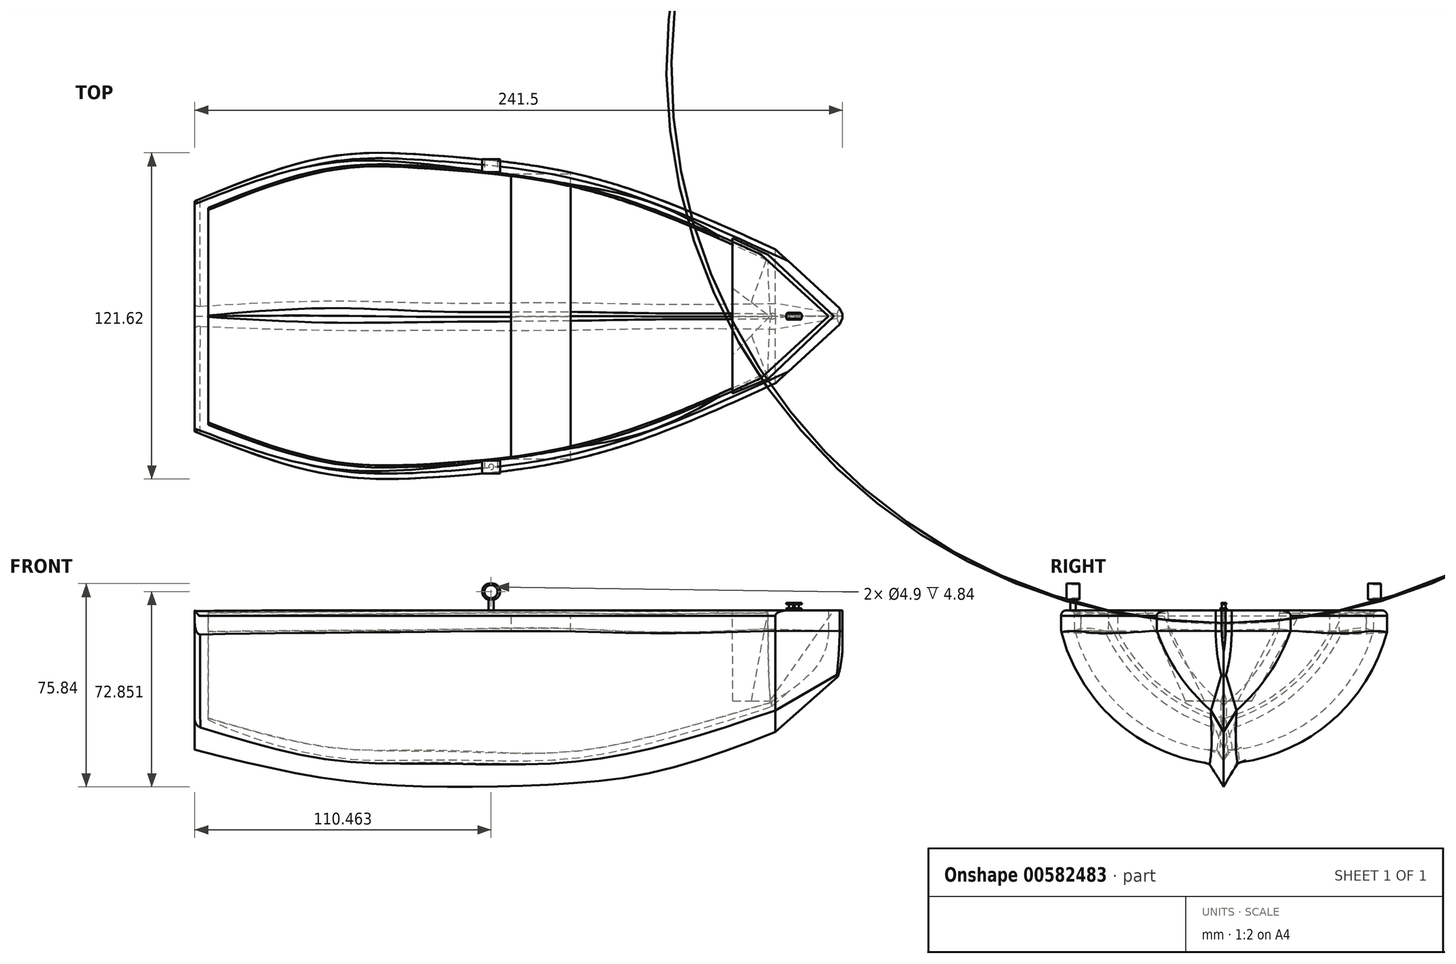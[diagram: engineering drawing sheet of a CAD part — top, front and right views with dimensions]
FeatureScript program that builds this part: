
annotation { "Feature Type Name" : "Feature", "Feature Type Description" : "" }
export const myFeature = defineFeature(function(context is Context, id is Id, definition is map)
    precondition{}
    {
        {
            var Q0;
            Q0=qCreatedBy(makeId("Right.planeOp"),FACE);
            var sketch = newSketch(context, id + "F0", { "sketchPlane" : qUnion([Q0])});
            skArc(sketch, "E0", {"start": v(-60, 57.64) * mm, "mid": v(-30.31, 51.1) * mm, "end": v(0, 48.9) * mm});
            skLineSegment(sketch, "E1", {"start": v(-59.87, 48.64) * mm, "end": v(-60, 57.64) * mm});
            skArc(sketch, "E2", {"start": v(-59.87, 48.64) * mm, "mid": v(-39.75, 16) * mm, "end": v(-5.17, -0.56) * mm});
            skArc(sketch, "E3.MirrorCS", {"start": v(60, 57.64) * mm, "mid": v(30.31, 51.1) * mm, "end": v(0, 48.9) * mm});
            skArc(sketch, "E4.MirrorCS", {"start": v(59.87, 48.64) * mm, "mid": v(39.55, 16.29) * mm, "end": v(4.98, 0) * mm});
            skLineSegment(sketch, "E5.MirrorCS", {"start": v(59.87, 48.64) * mm, "end": v(60, 57.64) * mm});
            skLineSegment(sketch, "E6", {"start": v(-5.17, -0.56) * mm, "end": v(0, -9.15) * mm});
            skLineSegment(sketch, "E7.MirrorCS", {"start": v(4.98, 0) * mm, "end": v(0, -9.15) * mm});
            skSolve(sketch);
        }
        {
            var Q0;
            {var subQ4=sQuery(id+"F0.wireOp",EDGE,"E1");Q0=makeQuery(id+"F0.imprint","IMPRINT",FACE,{"disambiguationData":[TD([[makeQuery(id+"F0.imprint","IMPRINT",EDGE,{"derivedFrom":subQ4}),-1.0]])]});}
            cPlane(context, id + "F1", {"entities" : qUnion([Q0]), "cplaneType" : CPlaneType.OFFSET, "offset" : 35 * mm, "oppositeDirection" : true, "width" : 150 * mm, "height" : 150 * mm});
        }
        {
            var Q0;
            Q0=qCreatedBy(id+"F1.planeOp",FACE);
            var sketch = newSketch(context, id + "F2", { "sketchPlane" : qUnion([Q0])});
            skArc(sketch, "E8", {"start": v(-59.74, 57.34) * mm, "mid": v(-30.06, 50.79) * mm, "end": v(0.26, 48.59) * mm});
            skLineSegment(sketch, "E9", {"start": v(-59.61, 48.34) * mm, "end": v(-59.74, 57.34) * mm});
            skArc(sketch, "E10", {"start": v(-59.61, 48.34) * mm, "mid": v(-39.35, 16.5) * mm, "end": v(-5.24, 0.36) * mm});
            skArc(sketch, "E11.MirrorCS", {"start": v(60.25, 57.34) * mm, "mid": v(30.57, 50.79) * mm, "end": v(0.26, 48.59) * mm});
            skArc(sketch, "E12.MirrorCS", {"start": v(60.13, 48.34) * mm, "mid": v(39.87, 16.5) * mm, "end": v(5.75, 0.36) * mm});
            skLineSegment(sketch, "E13.MirrorCS", {"start": v(60.13, 48.34) * mm, "end": v(60.25, 57.34) * mm});
            skLineSegment(sketch, "E14", {"start": v(-5.24, 0.36) * mm, "end": v(0, -6.9) * mm});
            skLineSegment(sketch, "E15.MirrorCS", {"start": v(5.75, 0.36) * mm, "end": v(5.75, 0.36) * mm});
            skLineSegment(sketch, "E16", {"start": v(5.75, 0.36) * mm, "end": v(0, -6.9) * mm});
            skSolve(sketch);
        }
        {
            var Q0;
            {var subQ4=sQuery(id+"F2.wireOp",EDGE,"E9");Q0=makeQuery(id+"F2.imprint","IMPRINT",FACE,{"disambiguationData":[TD([[makeQuery(id+"F2.imprint","IMPRINT",EDGE,{"derivedFrom":subQ4}),-1.0]])]});}
            cPlane(context, id + "F3", {"entities" : qUnion([Q0]), "cplaneType" : CPlaneType.OFFSET, "offset" : 55 * mm, "oppositeDirection" : true, "width" : 150 * mm, "height" : 150 * mm});
        }
        {
            var Q0;
            Q0=qCreatedBy(id+"F3.planeOp",FACE);
            var sketch = newSketch(context, id + "F4", { "sketchPlane" : qUnion([Q0])});
            skLineSegment(sketch, "E17", {"start": v(3.65, 13.62) * mm, "end": v(0, 4.64) * mm});
            skArc(sketch, "E18", {"start": v(-0.02, 51.89) * mm, "mid": v(21.6, 53.12) * mm, "end": v(42.98, 56.6) * mm});
            skArc(sketch, "E19.MirrorCS", {"start": v(0.02, 51.89) * mm, "mid": v(-21.6, 53.12) * mm, "end": v(-42.98, 56.6) * mm});
            skLineSegment(sketch, "E20.MirrorCS", {"start": v(-3.65, 13.62) * mm, "end": v(0, 4.64) * mm});
            skLineSegment(sketch, "E21", {"start": v(-42.98, 56.6) * mm, "end": v(-42.98, 47.6) * mm});
            skLineSegment(sketch, "E22", {"start": v(42.98, 56.6) * mm, "end": v(42.98, 47.6) * mm});
            skArc(sketch, "E23", {"start": v(3.65, 13.62) * mm, "mid": v(26.69, 26.7) * mm, "end": v(42.98, 47.6) * mm});
            skPoint(sketch, "E24.orphan", {"position": v(53.06, 38.96) * mm});
            skArc(sketch, "E25", {"start": v(-42.98, 47.6) * mm, "mid": v(-26.74, 26.64) * mm, "end": v(-3.65, 13.62) * mm});
            skPoint(sketch, "E26.orphan", {"position": v(-53.06, 38.96) * mm});
            skSolve(sketch);
        }
        {
            var Q0;
            Q0=qCreatedBy(makeId("Right.planeOp"),FACE);
            cPlane(context, id + "F5", {"entities" : qUnion([Q0]), "cplaneType" : CPlaneType.OFFSET, "offset" : 50 * mm, "width" : 150 * mm, "height" : 150 * mm});
        }
        {
            var Q0;
            Q0=qCreatedBy(id+"F5.planeOp",FACE);
            var sketch = newSketch(context, id + "F6", { "sketchPlane" : qUnion([Q0])});
            skArc(sketch, "E27", {"start": v(-53.66, 57.72) * mm, "mid": v(-27.06, 52.31) * mm, "end": v(0, 50.23) * mm});
            skLineSegment(sketch, "E28.MirrorCS", {"start": v(53.66, 57.72) * mm, "end": v(53.66, 48.72) * mm});
            skArc(sketch, "E29.MirrorCS", {"start": v(53.66, 57.72) * mm, "mid": v(27.06, 52.31) * mm, "end": v(0, 50.23) * mm});
            skLineSegment(sketch, "E30", {"start": v(-5.12, 0) * mm, "end": v(0, -7.9) * mm});
            skLineSegment(sketch, "E31", {"start": v(0, -7.9) * mm, "end": v(5.12, 0) * mm});
            skLineSegment(sketch, "E32", {"start": v(-53.66, 57.72) * mm, "end": v(-53.66, 48.72) * mm});
            skArc(sketch, "E33", {"start": v(5.12, 0) * mm, "mid": v(33.45, 20.31) * mm, "end": v(53.66, 48.72) * mm});
            skArc(sketch, "E34.MirrorCS", {"start": v(-5.12, 0) * mm, "mid": v(-33.45, 20.31) * mm, "end": v(-53.66, 48.72) * mm});
            skSolve(sketch);
        }
        {
            var Q0;
            Q0=qCreatedBy(id+"F5.planeOp",FACE);
            cPlane(context, id + "F7", {"entities" : qUnion([Q0]), "cplaneType" : CPlaneType.OFFSET, "offset" : 25 * mm, "width" : 150 * mm, "height" : 150 * mm});
        }
        {
            var Q0;
            Q0=qCreatedBy(id+"F7.planeOp",FACE);
            var sketch = newSketch(context, id + "F8", { "sketchPlane" : qUnion([Q0])});
            skLineSegment(sketch, "E35", {"start": v(0, -5.05) * mm, "end": v(-4.64, 3.9) * mm});
            skArc(sketch, "E36", {"start": v(-46.56, 57.11) * mm, "mid": v(-23.4, 53.26) * mm, "end": v(0, 51.52) * mm});
            skArc(sketch, "E37.MirrorCS", {"start": v(46.56, 57.11) * mm, "mid": v(23.4, 53.26) * mm, "end": v(0, 51.52) * mm});
            skLineSegment(sketch, "E38.MirrorCS", {"start": v(46.56, 57.11) * mm, "end": v(46.56, 48.11) * mm});
            skLineSegment(sketch, "E39.MirrorCS", {"start": v(0, -5.05) * mm, "end": v(4.64, 3.9) * mm});
            skLineSegment(sketch, "E40", {"start": v(-46.56, 57.11) * mm, "end": v(-46.56, 48.11) * mm});
            skArc(sketch, "E41", {"start": v(4.64, 3.9) * mm, "mid": v(31.6, 20.31) * mm, "end": v(46.56, 48.11) * mm});
            skArc(sketch, "E42.MirrorCS", {"start": v(-4.64, 3.9) * mm, "mid": v(-31.6, 20.31) * mm, "end": v(-46.56, 48.11) * mm});
            skSolve(sketch);
        }
        {
            var Q0;
            Q0=qCreatedBy(id+"F7.planeOp",FACE);
            cPlane(context, id + "F9", {"entities" : qUnion([Q0]), "cplaneType" : CPlaneType.OFFSET, "offset" : 51.5 * mm, "width" : 150 * mm, "height" : 150 * mm});
        }
        {
            var Q0;
            Q0=qCreatedBy(id+"F9.planeOp",FACE);
            var sketch = newSketch(context, id + "F10", { "sketchPlane" : qUnion([Q0])});
            skLineSegment(sketch, "E43", {"start": v(0, 11.2) * mm, "end": v(-4.78, 19.28) * mm});
            skLineSegment(sketch, "E44.MirrorCS", {"start": v(0, 11.2) * mm, "end": v(4.78, 19.28) * mm});
            skLineSegment(sketch, "E45", {"start": v(-25, 58.04) * mm, "end": v(0, 53.5) * mm});
            skLineSegment(sketch, "E46", {"start": v(0, 53.5) * mm, "end": v(25, 58.04) * mm});
            skLineSegment(sketch, "E47", {"start": v(-25, 58.04) * mm, "end": v(-25, 49.04) * mm});
            skArc(sketch, "E48", {"start": v(-25, 49.04) * mm, "mid": v(-16.81, 32.85) * mm, "end": v(-4.78, 19.28) * mm});
            skLineSegment(sketch, "E49", {"start": v(25, 58.04) * mm, "end": v(25, 49.04) * mm});
            skArc(sketch, "E50.MirrorCS", {"start": v(25, 49.04) * mm, "mid": v(16.81, 32.85) * mm, "end": v(4.78, 19.28) * mm});
            skSolve(sketch);
        }
        {
            var Q0;
            Q0=makeQuery(id+"F4.imprint","IMPRINT",FACE,{"disambiguationData":[TD([[makeQuery(id+"F4.imprint","IMPRINT",EDGE,{"derivedFrom":sQuery(id+"F4.wireOp",EDGE,"E17")}),-1.0]])]});
            var Q1;
            Q1=makeQuery(id+"F2.imprint","IMPRINT",FACE,{"disambiguationData":[TD([[makeQuery(id+"F2.imprint","IMPRINT",EDGE,{"derivedFrom":sQuery(id+"F2.wireOp",EDGE,"E9")}),-1.0]])]});
            var Q2;
            Q2=makeQuery(id+"F0.imprint","IMPRINT",FACE,{"disambiguationData":[TD([[makeQuery(id+"F0.imprint","IMPRINT",EDGE,{"derivedFrom":sQuery(id+"F0.wireOp",EDGE,"E1")}),-1.0]])]});
            var Q3;
            Q3=makeQuery(id+"F6.imprint","IMPRINT",FACE,{"disambiguationData":[TD([[makeQuery(id+"F6.imprint","IMPRINT",EDGE,{"derivedFrom":sQuery(id+"F6.wireOp",EDGE,"E27")}),-1.0]])]});
            var Q4;
            Q4=makeQuery(id+"F8.imprint","IMPRINT",FACE,{"disambiguationData":[TD([[makeQuery(id+"F8.imprint","IMPRINT",EDGE,{"derivedFrom":sQuery(id+"F8.wireOp",EDGE,"E35")}),-1.0]])]});
            var Q5;
            Q5=makeQuery(id+"F10.imprint","IMPRINT",FACE,{"disambiguationData":[TD([[makeQuery(id+"F10.imprint","IMPRINT",EDGE,{"derivedFrom":sQuery(id+"F10.wireOp",EDGE,"E43")}),-1.0]])]});
            loft(context, id + "F11", {"sheetProfilesArray" : [{ "sheetProfileEntities" : qUnion([Q0]) }, { "sheetProfileEntities" : qUnion([Q1]) }, { "sheetProfileEntities" : qUnion([Q2]) }, { "sheetProfileEntities" : qUnion([Q3]) }, { "sheetProfileEntities" : qUnion([Q4]) }, { "sheetProfileEntities" : qUnion([Q5]) }]});
        }
        {
            var Q0;
            Q0=makeQuery(id+"F11.opLoft","CAP_FACE",FACE,{"disambiguationData":[OSD([makeQuery(id+"F10.imprint","IMPRINT",FACE,{"disambiguationData":[TD([[makeQuery(id+"F10.imprint","IMPRINT",EDGE,{"derivedFrom":sQuery(id+"F10.wireOp",EDGE,"E43")}),-1.0]])]})])],"isStart":true});
            cPlane(context, id + "F12", {"entities" : qUnion([Q0]), "cplaneType" : CPlaneType.OFFSET, "offset" : 25 * mm, "width" : 150 * mm, "height" : 150 * mm});
        }
        {
            var Q0;
            Q0=qCreatedBy(id+"F12.planeOp",FACE);
            var sketch = newSketch(context, id + "F13", { "sketchPlane" : qUnion([Q0])});
            skLineSegment(sketch, "E51", {"start": v(-2.08, 48.78) * mm, "end": v(-2.08, 57.78) * mm});
            skLineSegment(sketch, "E52", {"start": v(-0.51, 33.77) * mm, "end": v(0, 33.28) * mm});
            skArc(sketch, "E53", {"start": v(-2.08, 57.78) * mm, "mid": v(-1.04, 57.74) * mm, "end": v(0, 57.72) * mm});
            skArc(sketch, "E54.MirrorCS", {"start": v(2.08, 57.78) * mm, "mid": v(1.04, 57.74) * mm, "end": v(0, 57.72) * mm});
            skLineSegment(sketch, "E55.MirrorCS", {"start": v(2.08, 48.78) * mm, "end": v(2.08, 57.78) * mm});
            skArc(sketch, "E56.MirrorCS", {"start": v(2.08, 48.78) * mm, "mid": v(1.64, 41.24) * mm, "end": v(0.51, 33.77) * mm});
            skLineSegment(sketch, "E57.MirrorCS", {"start": v(0.51, 33.77) * mm, "end": v(0, 33.28) * mm});
            skArc(sketch, "E58.MirrorCS", {"start": v(-2.08, 48.78) * mm, "mid": v(-1.64, 41.24) * mm, "end": v(-0.51, 33.77) * mm});
            skSolve(sketch);
        }
        {
            var Q1;
            Q1=makeQuery(id+"F13.imprint","IMPRINT",FACE,{"disambiguationData":[TD([[makeQuery(id+"F13.imprint","IMPRINT",EDGE,{"derivedFrom":sQuery(id+"F13.wireOp",EDGE,"E51")}),-1.0]])]});
            var Q2;
            Q2=makeQuery(id+"F11.opLoft","CAP_FACE",FACE,{"disambiguationData":[OSD([makeQuery(id+"F10.imprint","IMPRINT",FACE,{"disambiguationData":[TD([[makeQuery(id+"F10.imprint","IMPRINT",EDGE,{"derivedFrom":sQuery(id+"F10.wireOp",EDGE,"E43")}),-1.0]])]})])],"isStart":true});
            loft(context, id + "F14", {"operationType" : NewBodyOperationType.ADD, "sheetProfilesArray" : [{ "sheetProfileEntities" : qUnion([Q1]) }, { "sheetProfileEntities" : qUnion([Q2]) }]});
        }
        {
            var Q0;
            Q0=makeQuery(id+"F14.opLoft","MID_CAP_EDGE",EDGE,{"disambiguationData":[OSD([sQuery(id+"F13.wireOp",EDGE,"E51"),sQuery(id+"F13.wireOp",EDGE,"E53"),sQuery(id+"F13.wireOp",EDGE,"E58.MirrorCS")])],"capPos":0.0});
            var Q1;
            Q1=makeQuery(id+"F14.opLoft","MID_CAP_EDGE",EDGE,{"disambiguationData":[OSD([sQuery(id+"F13.wireOp",EDGE,"E54.MirrorCS"),sQuery(id+"F13.wireOp",EDGE,"E55.MirrorCS"),sQuery(id+"F13.wireOp",EDGE,"E56.MirrorCS")])],"capPos":0.0});
            var Q2;
            Q2=makeQuery(id+"F14.opLoft","MID_CAP_EDGE",EDGE,{"disambiguationData":[OSD([sQuery(id+"F13.wireOp",EDGE,"E51"),sQuery(id+"F13.wireOp",EDGE,"E52"),sQuery(id+"F13.wireOp",EDGE,"E58.MirrorCS")])],"capPos":0.0});
            var Q3;
            Q3=makeQuery(id+"F14.opLoft","MID_CAP_EDGE",EDGE,{"disambiguationData":[OSD([sQuery(id+"F13.wireOp",EDGE,"E55.MirrorCS"),sQuery(id+"F13.wireOp",EDGE,"E56.MirrorCS"),sQuery(id+"F13.wireOp",EDGE,"E57.MirrorCS")])],"capPos":0.0});
            chamfer(context, id + "F15", {"entities" : qUnion([Q0, Q1, Q2, Q3]), "width" : 3 * mm, "tangentPropagation" : true});
        }
        {
            var Q0;
            Q0=makeQuery(id+"F11.opLoft","SWEPT_FACE",FACE,{"disambiguationData":[OSD([sQuery(id+"F2.wireOp",EDGE,"E9"),sQuery(id+"F2.wireOp",EDGE,"E8"),sQuery(id+"F2.wireOp",EDGE,"E11.MirrorCS"),sQuery(id+"F4.wireOp",EDGE,"E18"),sQuery(id+"F4.wireOp",EDGE,"E19.MirrorCS"),sQuery(id+"F4.wireOp",EDGE,"E21")])]});
            var Q1;
            Q1=makeQuery(id+"F11.opLoft","SWEPT_FACE",FACE,{"disambiguationData":[OSD([sQuery(id+"F2.wireOp",EDGE,"E8"),sQuery(id+"F2.wireOp",EDGE,"E11.MirrorCS"),sQuery(id+"F2.wireOp",EDGE,"E13.MirrorCS"),sQuery(id+"F4.wireOp",EDGE,"E18"),sQuery(id+"F4.wireOp",EDGE,"E19.MirrorCS"),sQuery(id+"F4.wireOp",EDGE,"E22")])]});
            var Q2;
            Q2=makeQuery(id+"F14.opLoft","SWEPT_FACE",FACE,{"disambiguationData":[OSD([sQuery(id+"F10.wireOp",EDGE,"E45"),sQuery(id+"F10.wireOp",EDGE,"E46"),sQuery(id+"F10.wireOp",EDGE,"E49"),sQuery(id+"F13.wireOp",EDGE,"E53"),sQuery(id+"F13.wireOp",EDGE,"E54.MirrorCS"),sQuery(id+"F13.wireOp",EDGE,"E55.MirrorCS")])]});
            var Q3;
            Q3=makeQuery(id+"F14.opLoft","SWEPT_FACE",FACE,{"disambiguationData":[OSD([sQuery(id+"F10.wireOp",EDGE,"E45"),sQuery(id+"F10.wireOp",EDGE,"E46"),sQuery(id+"F10.wireOp",EDGE,"E47"),sQuery(id+"F13.wireOp",EDGE,"E51"),sQuery(id+"F13.wireOp",EDGE,"E53"),sQuery(id+"F13.wireOp",EDGE,"E54.MirrorCS")])]});
            shell(context, id + "F16", {"entities" : qUnion([Q0, Q1, Q2, Q3]), "thickness" : 5 * mm});
        }
        {
            var Q0;
            Q0=qCreatedBy(makeId("Top.planeOp"),FACE);
            cPlane(context, id + "F17", {"entities" : qUnion([Q0]), "cplaneType" : CPlaneType.OFFSET, "offset" : 16.8 * mm, "width" : 150 * mm, "height" : 150 * mm});
        }
        {
            var Q0;
            Q0=qCreatedBy(makeId("Front.planeOp"),FACE);
            var sketch = newSketch(context, id + "F18", { "sketchPlane" : qUnion([Q0])});
            skLineSegment(sketch, "E59", {"start": v(-90, 56.6) * mm, "end": v(151.58, 56.6) * mm});
            skLineSegment(sketch, "E60", {"start": v(151.58, 56.6) * mm, "end": v(157.85, 67.74) * mm});
            skLineSegment(sketch, "E61", {"start": v(157.85, 67.74) * mm, "end": v(-96.6, 64.76) * mm});
            skLineSegment(sketch, "E62", {"start": v(-96.6, 64.76) * mm, "end": v(-90, 56.6) * mm});
            skSolve(sketch);
        }
        {
            var Q0;
            Q0=makeQuery(id+"F18.imprint","IMPRINT",FACE,{"disambiguationData":[TD([[makeQuery(id+"F18.imprint","IMPRINT",EDGE,{"derivedFrom":sQuery(id+"F18.wireOp",EDGE,"E59")}),1.0]])]});
            extrude(context, id + "F19", {"entities" : qUnion([Q0]), "operationType" : NewBodyOperationType.REMOVE, "endBound" : BoundingType.SYMMETRIC, "depth" : 167.2 * mm, "offsetDistance" : 25 * mm});
        }
        {
            var Q0;
            Q0=makeQuery(id+"F11.opLoft","MID_CAP_EDGE",EDGE,{"disambiguationData":[OSD([sQuery(id+"F4.wireOp",EDGE,"E20.MirrorCS"),sQuery(id+"F4.wireOp",EDGE,"E21"),sQuery(id+"F4.wireOp",EDGE,"E25")])],"capPos":0.0});
            var Q1;
            Q1=makeQuery(id+"F11.opLoft","MID_CAP_EDGE",EDGE,{"disambiguationData":[OSD([sQuery(id+"F4.wireOp",EDGE,"E17"),sQuery(id+"F4.wireOp",EDGE,"E22"),sQuery(id+"F4.wireOp",EDGE,"E23")])],"capPos":0.0});
            fillet(context, id + "F20", {"entities" : qUnion([Q0, Q1]), "radius" : 3 * mm, "tangentPropagation" : true, "allowEdgeOverflow" : false});
        }
        {
            var Q0;
            Q0=makeQuery(id+"F19.boolean.opBoolean","INTERSECT",EDGE,{"derivedFrom":[makeQuery(id+"F11.opLoft","SWEPT_FACE",FACE,{"disambiguationData":[OSD([sQuery(id+"F2.wireOp",EDGE,"E11.MirrorCS"),sQuery(id+"F2.wireOp",EDGE,"E12.MirrorCS"),sQuery(id+"F2.wireOp",EDGE,"E13.MirrorCS"),sQuery(id+"F4.wireOp",EDGE,"E18"),sQuery(id+"F4.wireOp",EDGE,"E22"),sQuery(id+"F4.wireOp",EDGE,"E23")])]}),makeQuery(id+"F19.opExtrude","SWEPT_FACE",FACE,{"disambiguationData":[OSD([sQuery(id+"F18.wireOp",EDGE,"E59")])]})]});
            var Q1;
            Q1=makeQuery(id+"F19.boolean.opBoolean","INTERSECT",EDGE,{"derivedFrom":[makeQuery(id+"F11.opLoft","SWEPT_FACE",FACE,{"disambiguationData":[OSD([sQuery(id+"F2.wireOp",EDGE,"E9"),sQuery(id+"F2.wireOp",EDGE,"E10"),sQuery(id+"F2.wireOp",EDGE,"E8"),sQuery(id+"F4.wireOp",EDGE,"E19.MirrorCS"),sQuery(id+"F4.wireOp",EDGE,"E21"),sQuery(id+"F4.wireOp",EDGE,"E25")])]}),makeQuery(id+"F19.opExtrude","SWEPT_FACE",FACE,{"disambiguationData":[OSD([sQuery(id+"F18.wireOp",EDGE,"E59")])]})]});
            fillet(context, id + "F21", {"entities" : qUnion([Q0, Q1]), "radius" : 2 * mm, "tangentPropagation" : true, "allowEdgeOverflow" : false});
        }
        {
            var Q0;
            Q0=makeQuery(id+"F16.opShell","OFFSET_EDGE",EDGE,{"disambiguationData":[OSD([sQuery(id+"F0.wireOp",EDGE,"E1"),sQuery(id+"F0.wireOp",EDGE,"E0"),sQuery(id+"F2.wireOp",EDGE,"E9"),sQuery(id+"F2.wireOp",EDGE,"E8"),sQuery(id+"F4.wireOp",EDGE,"E19.MirrorCS"),sQuery(id+"F4.wireOp",EDGE,"E21"),sQuery(id+"F6.wireOp",EDGE,"E27"),sQuery(id+"F6.wireOp",EDGE,"E32"),sQuery(id+"F8.wireOp",EDGE,"E36"),sQuery(id+"F8.wireOp",EDGE,"E40"),sQuery(id+"F10.wireOp",EDGE,"E45"),sQuery(id+"F10.wireOp",EDGE,"E47")])]});
            var Q1;
            Q1=makeQuery(id+"F19.boolean.opBoolean","INTERSECT",EDGE,{"derivedFrom":[makeQuery(id+"F16.opShell","OFFSET_FACE",FACE,{"disambiguationData":[OSD([sQuery(id+"F2.wireOp",EDGE,"E9"),sQuery(id+"F2.wireOp",EDGE,"E10"),sQuery(id+"F2.wireOp",EDGE,"E8"),sQuery(id+"F4.wireOp",EDGE,"E19.MirrorCS"),sQuery(id+"F4.wireOp",EDGE,"E21"),sQuery(id+"F4.wireOp",EDGE,"E25")])]}),makeQuery(id+"F19.opExtrude","SWEPT_FACE",FACE,{"disambiguationData":[OSD([sQuery(id+"F18.wireOp",EDGE,"E59")])]})]});
            var Q2;
            Q2=makeQuery(id+"F19.boolean.opBoolean","INTERSECT",EDGE,{"derivedFrom":[makeQuery(id+"F16.opShell","OFFSET_FACE",FACE,{"disambiguationData":[OSD([sQuery(id+"F2.wireOp",EDGE,"E11.MirrorCS"),sQuery(id+"F2.wireOp",EDGE,"E12.MirrorCS"),sQuery(id+"F2.wireOp",EDGE,"E13.MirrorCS"),sQuery(id+"F4.wireOp",EDGE,"E18"),sQuery(id+"F4.wireOp",EDGE,"E22"),sQuery(id+"F4.wireOp",EDGE,"E23")])]}),makeQuery(id+"F19.opExtrude","SWEPT_FACE",FACE,{"disambiguationData":[OSD([sQuery(id+"F18.wireOp",EDGE,"E59")])]})]});
            var Q3;
            Q3=makeQuery(id+"F16.opShell","OFFSET_EDGE",EDGE,{"disambiguationData":[OSD([sQuery(id+"F0.wireOp",EDGE,"E3.MirrorCS"),sQuery(id+"F0.wireOp",EDGE,"E5.MirrorCS"),sQuery(id+"F2.wireOp",EDGE,"E11.MirrorCS"),sQuery(id+"F2.wireOp",EDGE,"E13.MirrorCS"),sQuery(id+"F4.wireOp",EDGE,"E18"),sQuery(id+"F4.wireOp",EDGE,"E22"),sQuery(id+"F6.wireOp",EDGE,"E28.MirrorCS"),sQuery(id+"F6.wireOp",EDGE,"E29.MirrorCS"),sQuery(id+"F8.wireOp",EDGE,"E37.MirrorCS"),sQuery(id+"F8.wireOp",EDGE,"E38.MirrorCS"),sQuery(id+"F10.wireOp",EDGE,"E46"),sQuery(id+"F10.wireOp",EDGE,"E49")])]});
            fillet(context, id + "F22", {"entities" : qUnion([Q0, Q1, Q2, Q3]), "radius" : 1 * mm, "tangentPropagation" : true, "allowEdgeOverflow" : false});
        }
        {
            var Q0;
            Q0=makeQuery(id+"F19.boolean.opBoolean","COPY",FACE,{"derivedFrom":makeQuery(id+"F19.opExtrude","SWEPT_FACE",FACE,{"disambiguationData":[OSD([sQuery(id+"F18.wireOp",EDGE,"E59")])]})});
            cPlane(context, id + "F23", {"entities" : qUnion([Q0]), "cplaneType" : CPlaneType.OFFSET, "offset" : 0 * mm, "width" : 150 * mm, "height" : 150 * mm});
        }
        {
            var Q0;
            Q0=qCreatedBy(id+"F17.planeOp",FACE);
            cPlane(context, id + "F24", {"entities" : qUnion([Q0]), "cplaneType" : CPlaneType.OFFSET, "offset" : 6 * mm, "width" : 150 * mm, "height" : 150 * mm});
        }
        {
            var Q0;
            Q0=qCreatedBy(id+"F24.planeOp",FACE);
            var sketch = newSketch(context, id + "F25", { "sketchPlane" : qUnion([Q0])});
            skLineSegment(sketch, "E63", {"start": v(110.65, -14.26) * mm, "end": v(110.65, 10.52) * mm});
            skLineSegment(sketch, "E64", {"start": v(110.65, 10.52) * mm, "end": v(124.47, 0) * mm});
            skLineSegment(sketch, "E65", {"start": v(124.47, 0) * mm, "end": v(110.65, -14.26) * mm});
            skSolve(sketch);
        }
        {
            var Q0;
            Q0=qCreatedBy(id+"F23.planeOp",FACE);
            var sketch = newSketch(context, id + "F26", { "sketchPlane" : qUnion([Q0])});
            skLineSegment(sketch, "E66", {"start": v(110.48, -28.78) * mm, "end": v(110.48, 29.17) * mm});
            skLineSegment(sketch, "E67", {"start": v(110.48, 29.17) * mm, "end": v(123.82, 22.97) * mm});
            skLineSegment(sketch, "E68", {"start": v(123.82, 22.97) * mm, "end": v(148.35, 0) * mm});
            skLineSegment(sketch, "E69", {"start": v(148.35, 0) * mm, "end": v(123.82, -23.25) * mm});
            skLineSegment(sketch, "E70", {"start": v(123.82, -23.25) * mm, "end": v(110.48, -28.78) * mm});
            skSolve(sketch);
        }
        {
            var Q1;
            Q1 = qSketchRegion(id + "F25", true);
            var Q2;
            Q2 = qSketchRegion(id + "F26", true);
            loft(context, id + "F27", {"sheetProfilesArray" : [{ "sheetProfileEntities" : qUnion([Q1]) }, { "sheetProfileEntities" : qUnion([Q2]) }]});
        }
        {
            var Q0;
            Q0=makeQuery(id+"F27.boolean.opBoolean","MERGE",FACE,{"derivedFrom":[makeQuery(id+"F19.boolean.opBoolean","COPY",FACE,{"derivedFrom":makeQuery(id+"F19.opExtrude","SWEPT_FACE",FACE,{"disambiguationData":[OSD([sQuery(id+"F18.wireOp",EDGE,"E59")])]})}),makeQuery(id+"F27.opLoft","CAP_FACE",FACE,{"disambiguationData":[OSD([makeQuery(id+"F26.imprint","IMPRINT",FACE,{"disambiguationData":[TD([[makeQuery(id+"F26.imprint","IMPRINT",EDGE,{"derivedFrom":sQuery(id+"F26.wireOp",EDGE,"E66")}),-1.0]])]})])],"isStart":true})]});
            var sketch = newSketch(context, id + "F28", { "sketchPlane" : qUnion([Q0])});
            skLineSegment(sketch, "E71", {"start": v(130.63, 0) * mm, "end": v(130.63, 1.27) * mm});
            skLineSegment(sketch, "E72", {"start": v(130.63, 1.27) * mm, "end": v(130.63, -1.23) * mm});
            skLineSegment(sketch, "E73", {"start": v(130.63, -1.23) * mm, "end": v(136.23, -1.23) * mm});
            skLineSegment(sketch, "E74", {"start": v(136.23, -1.23) * mm, "end": v(136.23, 1.27) * mm});
            skLineSegment(sketch, "E75", {"start": v(136.23, 1.27) * mm, "end": v(130.63, 1.27) * mm});
            skSolve(sketch);
        }
        {
            var Q0;
            {var subQ0=sQuery(id+"F28.wireOp",EDGE,"E73");Q0=makeQuery(id+"F28.imprint","IMPRINT",FACE,{"disambiguationData":[TD([[makeQuery(id+"F28.imprint","IMPRINT",EDGE,{"derivedFrom":subQ0}),1.0]])]});}
            extrude(context, id + "F29", {"entities" : qUnion([Q0]), "depth" : 0.8 * mm, "offsetDistance" : 25 * mm});
        }
        {
            var Q0;
            Q0=makeQuery(id+"F29.opExtrude","CAP_FACE",FACE,{"disambiguationData":[OSD([sQuery(id+"F28.wireOp",EDGE,"E72"),sQuery(id+"F28.wireOp",EDGE,"E73"),sQuery(id+"F28.wireOp",EDGE,"E74"),sQuery(id+"F28.wireOp",EDGE,"E75")])],"isStart":false});
            var sketch = newSketch(context, id + "F30", { "sketchPlane" : qUnion([Q0])});
            skCircle(sketch, "E76", {"center": v(132.33, 0) * mm, "radius": 0.75 * mm});
            skCircle(sketch, "E77", {"center": v(134.53, 0) * mm, "radius": 0.75 * mm});
            skPoint(sketch, "E78.orphan", {"position": v(130.63, 0.02) * mm});
            skPoint(sketch, "E79.start.orphan", {"position": v(136.23, 0) * mm});
            skSolve(sketch);
        }
        {
            var Q0;
            Q0=makeQuery(id+"F30.imprint","IMPRINT",FACE,{"disambiguationData":[TD([[makeQuery(id+"F30.imprint","IMPRINT",EDGE,{"derivedFrom":sQuery(id+"F30.wireOp",EDGE,"E77")}),1.0]])]});
            var Q1;
            Q1=makeQuery(id+"F30.imprint","IMPRINT",FACE,{"disambiguationData":[TD([[makeQuery(id+"F30.imprint","IMPRINT",EDGE,{"derivedFrom":sQuery(id+"F30.wireOp",EDGE,"E76")}),1.0]])]});
            extrude(context, id + "F31", {"entities" : qUnion([Q0, Q1]), "operationType" : NewBodyOperationType.ADD, "depth" : 1.5 * mm, "offsetDistance" : 25 * mm});
        }
        {
            var Q0;
            Q0=makeQuery(id+"F31.opExtrude","CAP_FACE",FACE,{"disambiguationData":[OSD([sQuery(id+"F30.wireOp",EDGE,"E77")])],"isStart":false});
            var sketch = newSketch(context, id + "F32", { "sketchPlane" : qUnion([Q0])});
            skLineSegment(sketch, "E80", {"start": v(130.56, -0.87) * mm, "end": v(136.36, -0.87) * mm});
            skLineSegment(sketch, "E81", {"start": v(130.56, -0.87) * mm, "end": v(130.56, 0.87) * mm});
            skLineSegment(sketch, "E82", {"start": v(130.56, 0.87) * mm, "end": v(136.36, 0.9) * mm});
            skLineSegment(sketch, "E83", {"start": v(136.36, 0.9) * mm, "end": v(136.36, -0.87) * mm});
            skSolve(sketch);
        }
        {
            var Q0;
            Q0=makeQuery(id+"F32.imprint","IMPRINT",FACE,{"disambiguationData":[TD([[makeQuery(id+"F32.imprint","IMPRINT",EDGE,{"derivedFrom":sQuery(id+"F32.wireOp",EDGE,"E80")}),1.0]])]});
            var Q1;
            Q1=makeQuery(id+"F32.imprint","IMPRINT",FACE,{"disambiguationData":[TD([[makeQuery(id+"F32.imprint","IMPRINT",EDGE,{"derivedFrom":makeQuery(id+"F31.opExtrude","CAP_EDGE",EDGE,{"disambiguationData":[OSD([sQuery(id+"F30.wireOp",EDGE,"E77")])],"isStart":false})}),1.0]])]});
            extrude(context, id + "F33", {"entities" : qUnion([Q0, Q1]), "operationType" : NewBodyOperationType.ADD, "depth" : 0.45 * mm, "offsetDistance" : 25 * mm});
        }
        {
            var Q0;
            Q0=makeQuery(id+"F33.opExtrude","SWEPT_EDGE",EDGE,{"disambiguationData":[OSD([sQuery(id+"F32.wireOp",EDGE,"E80"),sQuery(id+"F32.wireOp",EDGE,"E81")])]});
            var Q1;
            Q1=makeQuery(id+"F33.opExtrude","SWEPT_EDGE",EDGE,{"disambiguationData":[OSD([sQuery(id+"F32.wireOp",EDGE,"E80"),sQuery(id+"F32.wireOp",EDGE,"E83")])]});
            var Q2;
            Q2=makeQuery(id+"F33.opExtrude","SWEPT_EDGE",EDGE,{"disambiguationData":[OSD([sQuery(id+"F32.wireOp",EDGE,"E81"),sQuery(id+"F32.wireOp",EDGE,"E82")])]});
            var Q3;
            Q3=makeQuery(id+"F33.opExtrude","SWEPT_EDGE",EDGE,{"disambiguationData":[OSD([sQuery(id+"F32.wireOp",EDGE,"E82"),sQuery(id+"F32.wireOp",EDGE,"E83")])]});
            var Q4;
            Q4=makeQuery(id+"F29.opExtrude","SWEPT_EDGE",EDGE,{"disambiguationData":[OSD([sQuery(id+"F28.wireOp",EDGE,"E74"),sQuery(id+"F28.wireOp",EDGE,"E75")])]});
            var Q5;
            Q5=makeQuery(id+"F29.opExtrude","SWEPT_EDGE",EDGE,{"disambiguationData":[OSD([sQuery(id+"F28.wireOp",EDGE,"E73"),sQuery(id+"F28.wireOp",EDGE,"E74")])]});
            var Q6;
            Q6=makeQuery(id+"F29.opExtrude","SWEPT_EDGE",EDGE,{"disambiguationData":[OSD([sQuery(id+"F28.wireOp",EDGE,"E72"),sQuery(id+"F28.wireOp",EDGE,"E75")])]});
            var Q7;
            Q7=makeQuery(id+"F29.opExtrude","SWEPT_EDGE",EDGE,{"disambiguationData":[OSD([sQuery(id+"F28.wireOp",EDGE,"E72"),sQuery(id+"F28.wireOp",EDGE,"E73")])]});
            fillet(context, id + "F34", {"entities" : qUnion([Q0, Q1, Q2, Q3, Q4, Q5, Q6, Q7]), "radius" : 0.5 * mm, "tangentPropagation" : true, "allowEdgeOverflow" : false});
        }
        {
            var Q0;
            Q0=qCreatedBy(makeId("Front.planeOp"),FACE);
            cPlane(context, id + "F35", {"entities" : qUnion([Q0]), "cplaneType" : CPlaneType.OFFSET, "offset" : 0 * mm, "width" : 150 * mm, "height" : 150 * mm});
        }
        {
            var Q0;
            Q0=qCreatedBy(id+"F35.planeOp",FACE);
            var sketch = newSketch(context, id + "F36", { "sketchPlane" : qUnion([Q0])});
            skLineSegment(sketch, "E84", {"start": v(50.18, 48.8) * mm, "end": v(50.18, 54.56) * mm});
            skLineSegment(sketch, "E85", {"start": v(50.18, 54.56) * mm, "end": v(27.97, 54.56) * mm});
            skLineSegment(sketch, "E86", {"start": v(27.97, 54.56) * mm, "end": v(27.97, 49) * mm});
            skLineSegment(sketch, "E87", {"start": v(27.97, 49) * mm, "end": v(50.18, 48.8) * mm});
            skSolve(sketch);
        }
        {
            var Q0;
            Q0=makeQuery(id+"F36.imprint","IMPRINT",FACE,{"disambiguationData":[TD([[makeQuery(id+"F36.imprint","IMPRINT",EDGE,{"derivedFrom":sQuery(id+"F36.wireOp",EDGE,"E84")}),1.0]])]});
            extrude(context, id + "F37", {"entities" : qUnion([Q0]), "endBound" : BoundingType.SYMMETRIC, "depth" : 106.4 * mm, "offsetDistance" : 25 * mm});
        }
        {
            var Q0;
            Q0=qCreatedBy(makeId("Top.planeOp"),FACE);
            cPlane(context, id + "F38", {"entities" : qUnion([Q0]), "cplaneType" : CPlaneType.OFFSET, "offset" : 56.6 * mm, "width" : 150 * mm, "height" : 150 * mm});
        }
        {
            var Q0;
            Q0=qCreatedBy(id+"F38.planeOp",FACE);
            var sketch = newSketch(context, id + "F39", { "sketchPlane" : qUnion([Q0])});
            skCircle(sketch, "E88.MirrorC", {"center": v(20.53, 56.17) * mm, "radius": 1 * mm});
            skCircle(sketch, "E89.MirrorC", {"center": v(20.53, -56.17) * mm, "radius": 1 * mm});
            skSolve(sketch);
        }
        {
            var Q0;
            Q0=makeQuery(id+"F39.imprint","IMPRINT",FACE,{"disambiguationData":[TD([[makeQuery(id+"F39.imprint","IMPRINT",EDGE,{"derivedFrom":sQuery(id+"F39.wireOp",EDGE,"E88.MirrorC")}),-1.0]])]});
            var Q1;
            Q1=makeQuery(id+"F39.imprint","IMPRINT",FACE,{"disambiguationData":[TD([[makeQuery(id+"F39.imprint","IMPRINT",EDGE,{"derivedFrom":sQuery(id+"F39.wireOp",EDGE,"E89.MirrorC")}),1.0]])]});
            extrude(context, id + "F40", {"entities" : qUnion([Q0, Q1]), "depth" : 4 * mm, "offsetDistance" : 25 * mm});
        }
        {
            var Q0;
            Q0=makeQuery(id+"F40.opExtrude","CAP_FACE",FACE,{"disambiguationData":[OSD([sQuery(id+"F39.wireOp",EDGE,"E89.MirrorC")])],"isStart":false});
            var sketch = newSketch(context, id + "F41", { "sketchPlane" : qUnion([Q0])});
            skLineSegment(sketch, "E90.bottom", {"start": v(17.22, -53.75) * mm, "end": v(23.84, -53.75) * mm});
            skLineSegment(sketch, "E90.top", {"start": v(17.22, -58.59) * mm, "end": v(23.84, -58.59) * mm});
            skLineSegment(sketch, "E90.left", {"start": v(17.22, -53.75) * mm, "end": v(17.22, -58.59) * mm});
            skLineSegment(sketch, "E90.right", {"start": v(23.84, -53.75) * mm, "end": v(23.84, -58.59) * mm});
            skPoint(sketch, "E90.middle", {"position": v(20.53, -56.17) * mm});
            skLineSegment(sketch, "E91.MirrorCS", {"start": v(17.22, 58.59) * mm, "end": v(23.84, 58.59) * mm});
            skLineSegment(sketch, "E92.MirrorCS", {"start": v(23.84, 53.75) * mm, "end": v(23.84, 58.59) * mm});
            skLineSegment(sketch, "E93.MirrorCS", {"start": v(17.22, 53.75) * mm, "end": v(23.84, 53.75) * mm});
            skLineSegment(sketch, "E94.MirrorCS", {"start": v(17.22, 53.75) * mm, "end": v(17.22, 58.59) * mm});
            skSolve(sketch);
        }
        {
            var Q0;
            Q0=makeQuery(id+"F41.imprint","IMPRINT",FACE,{"disambiguationData":[TD([[makeQuery(id+"F41.imprint","IMPRINT",EDGE,{"derivedFrom":sQuery(id+"F41.wireOp",EDGE,"E90.bottom")}),-1.0]])]});
            var Q1;
            Q1=makeQuery(id+"F41.imprint","IMPRINT",FACE,{"disambiguationData":[TD([[makeQuery(id+"F41.imprint","IMPRINT",EDGE,{"derivedFrom":makeQuery(id+"F40.opExtrude","CAP_EDGE",EDGE,{"disambiguationData":[OSD([sQuery(id+"F39.wireOp",EDGE,"E89.MirrorC")])],"isStart":false})}),1.0]])]});
            var Q2;
            Q2=makeQuery(id+"F41.imprint","IMPRINT",FACE,{"disambiguationData":[TD([[makeQuery(id+"F41.imprint","IMPRINT",EDGE,{"derivedFrom":sQuery(id+"F41.wireOp",EDGE,"E91.MirrorCS")}),-1.0]])]});
            extrude(context, id + "F42", {"entities" : qUnion([Q0, Q1, Q2]), "depth" : 6 * mm, "offsetDistance" : 25 * mm});
        }
        {
            var Q0;
            Q0=makeQuery(id+"F42.opExtrude","CAP_EDGE",EDGE,{"disambiguationData":[OSD([sQuery(id+"F41.wireOp",EDGE,"E90.right")])],"isStart":false});
            var Q1;
            Q1=makeQuery(id+"F42.opExtrude","CAP_EDGE",EDGE,{"disambiguationData":[OSD([sQuery(id+"F41.wireOp",EDGE,"E90.right")])],"isStart":true});
            var Q2;
            Q2=makeQuery(id+"F42.opExtrude","CAP_EDGE",EDGE,{"disambiguationData":[OSD([sQuery(id+"F41.wireOp",EDGE,"E90.left")])],"isStart":true});
            var Q3;
            Q3=makeQuery(id+"F42.opExtrude","CAP_EDGE",EDGE,{"disambiguationData":[OSD([sQuery(id+"F41.wireOp",EDGE,"E90.left")])],"isStart":false});
            fillet(context, id + "F43", {"entities" : qUnion([Q0, Q1, Q2, Q3]), "radius" : 2.87 * mm, "tangentPropagation" : true, "allowEdgeOverflow" : false});
        }
        {
            var Q0;
            Q0=makeQuery(id+"F42.opExtrude","SWEPT_FACE",FACE,{"disambiguationData":[OSD([sQuery(id+"F41.wireOp",EDGE,"E90.top")])]});
            var sketch = newSketch(context, id + "F44", { "sketchPlane" : qUnion([Q0])});
            skCircle(sketch, "E95", {"center": v(20.46, 63.61) * mm, "radius": 2.45 * mm});
            skSolve(sketch);
        }
        {
            var Q0;
            Q0=makeQuery(id+"F44.imprint","IMPRINT",FACE,{"disambiguationData":[TD([[makeQuery(id+"F44.imprint","IMPRINT",EDGE,{"derivedFrom":sQuery(id+"F44.wireOp",EDGE,"E95")}),1.0]])]});
            extrude(context, id + "F45", {"entities" : qUnion([Q0]), "operationType" : NewBodyOperationType.REMOVE, "oppositeDirection" : true, "depth" : 123.9 * mm, "offsetDistance" : 25 * mm});
        }
        {
            var Q0;
            Q0=makeQuery(id+"F42.opExtrude","CAP_EDGE",EDGE,{"disambiguationData":[OSD([sQuery(id+"F41.wireOp",EDGE,"E94.MirrorCS")])],"isStart":false});
            var Q1;
            Q1=makeQuery(id+"F42.opExtrude","CAP_EDGE",EDGE,{"disambiguationData":[OSD([sQuery(id+"F41.wireOp",EDGE,"E94.MirrorCS")])],"isStart":true});
            var Q2;
            Q2=makeQuery(id+"F42.opExtrude","CAP_EDGE",EDGE,{"disambiguationData":[OSD([sQuery(id+"F41.wireOp",EDGE,"E92.MirrorCS")])],"isStart":false});
            var Q3;
            Q3=makeQuery(id+"F42.opExtrude","CAP_EDGE",EDGE,{"disambiguationData":[OSD([sQuery(id+"F41.wireOp",EDGE,"E92.MirrorCS")])],"isStart":true});
            fillet(context, id + "F46", {"entities" : qUnion([Q0, Q1, Q2, Q3]), "radius" : 2.92 * mm, "tangentPropagation" : true, "allowEdgeOverflow" : false});
        }
        {
            var Q0;
            Q0=makeQuery(id+"F42.opExtrude","SWEPT_FACE",FACE,{"disambiguationData":[OSD([sQuery(id+"F41.wireOp",EDGE,"E93.MirrorCS")])]});
            var sketch = newSketch(context, id + "F47", { "sketchPlane" : qUnion([Q0])});
            skCircle(sketch, "E96", {"center": v(20.47, 63.6) * mm, "radius": 2.43 * mm});
            skSolve(sketch);
        }
        {
            var Q0;
            Q0=makeQuery(id+"F47.imprint","IMPRINT",FACE,{"disambiguationData":[TD([[makeQuery(id+"F47.imprint","IMPRINT",EDGE,{"derivedFrom":sQuery(id+"F47.wireOp",EDGE,"E96")}),1.0]])]});
            extrude(context, id + "F48", {"entities" : qUnion([Q0]), "operationType" : NewBodyOperationType.REMOVE, "oppositeDirection" : true, "depth" : 25 * mm, "offsetDistance" : 25 * mm});
        }
    });
